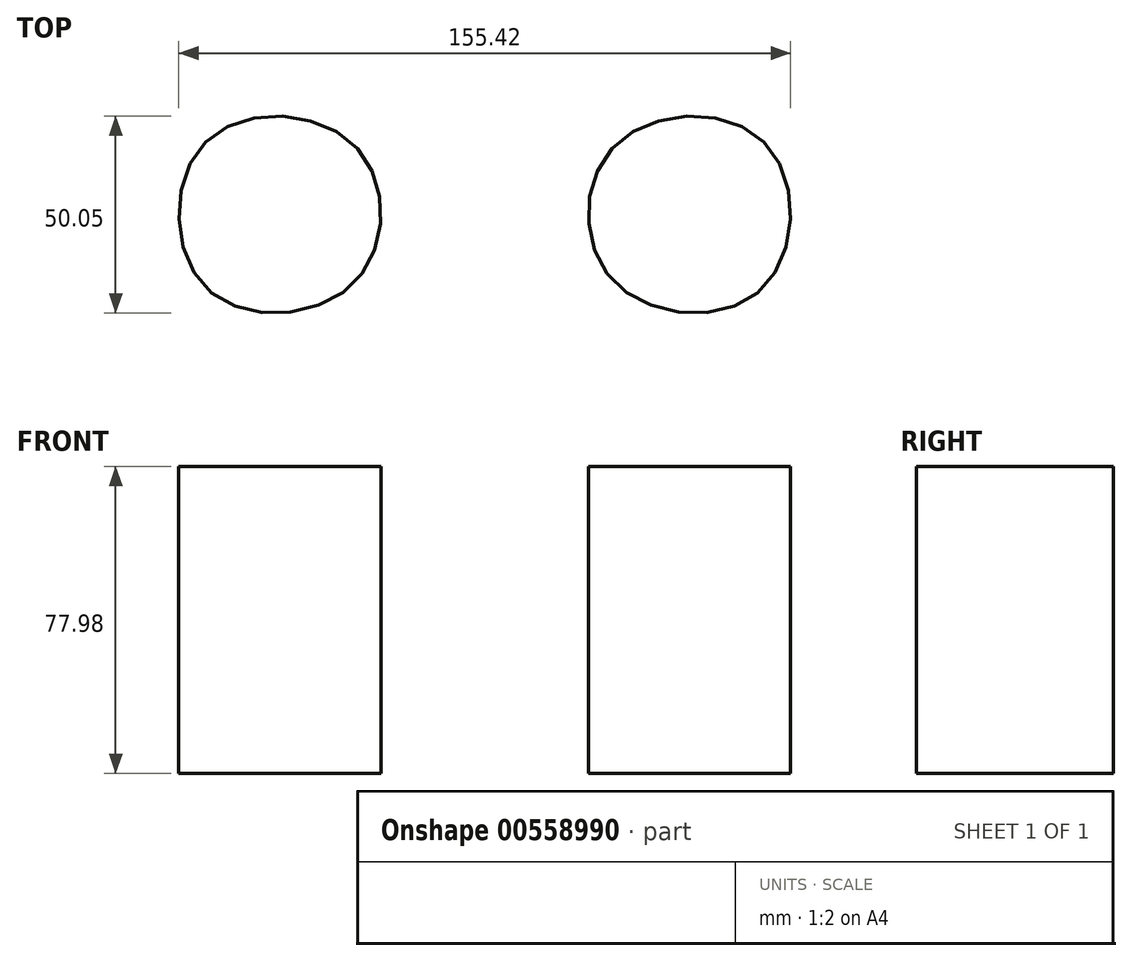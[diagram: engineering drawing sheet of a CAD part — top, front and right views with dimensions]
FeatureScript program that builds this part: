
annotation { "Feature Type Name" : "Feature", "Feature Type Description" : "" }
export const myFeature = defineFeature(function(context is Context, id is Id, definition is map)
    precondition{}
    {
        {
            var Q0;
            Q0=qCreatedBy(makeId("Top.planeOp"),FACE);
            var sketch = newSketch(context, id + "F0", { "sketchPlane" : qUnion([Q0])});
            skFitSpline(sketch, "E0", {"points": [v(-70.92, 68.26) * mm, v(-33.15, 67.42) * mm, v(-32.87, 32.73) * mm, v(-70.36, 30.77) * mm, v(-70.92, 68.26) * mm]});
            skFitSpline(sketch, "E1", {"points": [v(29.51, 66.86) * mm, v(68.4, 65.46) * mm, v(70.64, 24.06) * mm, v(27.56, 23.78) * mm, v(29.51, 66.86) * mm]});
            skSolve(sketch);
        }
        {
            var Q0;
            Q0=makeQuery(id+"F0.imprint","IMPRINT",FACE,{"disambiguationData":[TD([[makeQuery(id+"F0.imprint","IMPRINT",EDGE,{"derivedFrom":sQuery(id+"F0.wireOp",EDGE,"E0")}),-1.0]])]});
            extrude(context, id + "F1", {"entities" : qUnion([Q0]), "depth" : 77.98 * mm, "offsetDistance" : 25.4 * mm});
        }
        {
            var Q0;
            Q0=makeQuery(id+"F1.opExtrude","SWEPT_BODY",BODY,{"disambiguationData":[OSD([sQuery(id+"F0.wireOp",EDGE,"E0")])]});
            var Q1;
            Q1=qCreatedBy(makeId("Right.planeOp"),FACE);
            mirror(context, id + "F2", {"entities" : qUnion([Q0]), "mirrorPlane" : qUnion([Q1])});
        }
    });
